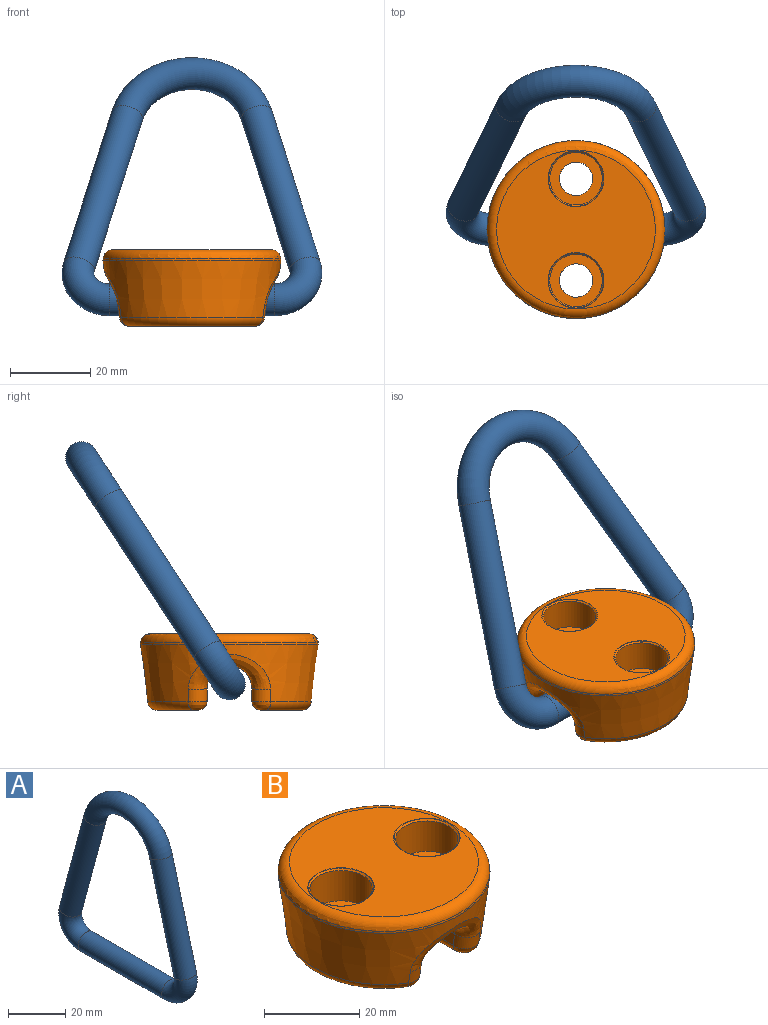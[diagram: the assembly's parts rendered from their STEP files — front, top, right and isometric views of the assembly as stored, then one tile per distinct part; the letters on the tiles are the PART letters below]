
ASSEMBLY  parts=2 mates=1
PART A: 6 faces, bbox 7.9x66.8x78.1 mm
  f0: cylinder r=3.97mm len=47.18mm, axis (0,0.26,0.97), area 1164.9mm2, adj f1,f5
  f1: torus R=7.94mm, axis (-1,0,0), area 362.7mm2, adj f0,f2
  f2: cylinder r=3.97mm len=41.05mm, axis (0,-1,0), area 1023.6mm2, adj f1,f3
  f3: torus R=7.94mm, axis (-1,0,0), area 362.7mm2, adj f2,f4
  f4: cylinder r=3.97mm len=47.18mm, axis (0,0.26,-0.97), area 1164.9mm2, adj f3,f5
  f5: torus R=16.67mm, axis (1,0,0), area 1088.2mm2, adj f0,f4
PART B: 44 faces, bbox 48x48x32 mm
  f0: plane 39.61x39.61mm, normal (0,0,1), area 926.8mm2, adj f22,f42,f43
  f1: cylinder r=5.56mm len=30.74mm, axis (0,1,0), area 274.6mm2, adj f6,f7,f9,f12,f32,f33,f34,f35
  f2: plane 31.44x10.14mm, normal (0,0,-1), area 170mm2, adj f14,f15,f16,f17,f39
  f3: cone r=22.23mm half-angle=7deg, axis (0,0,-1), area 63.1mm2, adj f4,f22
  f4: cone r=22.23mm half-angle=7deg, axis (0,0,1), area 1520.3mm2, adj f3,f8,f9,f10,f11,f12,f13,f16
  f5: plane 31.44x10.14mm, normal (0,0,-1), area 170mm2, adj f18,f19,f20,f21,f38
  f6: plane 30.74x3.18mm, normal (1,0,0), area 96.2mm2, adj f1,f8,f13,f15
  f7: plane 30.74x3.18mm, normal (-1,0,0), area 96.2mm2, adj f1,f10,f11,f20
  f8: bspline ~26.1x8.53mm, area 21mm2, adj f4,f6,f9,f17
  f9: bspline ~20.6x10.49mm, area 128mm2, adj f1,f4,f8,f10
  f10: bspline ~32.03x9.37mm, area 20.9mm2, adj f4,f7,f9,f21
  f11: bspline ~26.1x8.53mm, area 21mm2, adj f4,f7,f12,f18
  f12: bspline ~20.6x10.49mm, area 128mm2, adj f1,f4,f11,f13
  f13: bspline ~32.03x9.37mm, area 20.9mm2, adj f4,f6,f12,f14
  f14: bspline ~5.36x3.34mm, area 16.6mm2, adj f2,f13,f15,f16
  f15: cylinder r=2.39mm len=29.84mm, axis (0,-1,0), area 111.9mm2, adj f2,f6,f14,f17
  f16: torus R=18.09mm, axis (0,0,-1), area 140.7mm2, adj f2,f4,f14,f17
  f17: bspline ~5.37x3.89mm, area 16.6mm2, adj f2,f8,f15,f16
  f18: bspline ~5.37x3.89mm, area 16.6mm2, adj f5,f11,f19,f20
  f19: torus R=18.09mm, axis (0,0,-1), area 140.7mm2, adj f4,f5,f18,f21
  f20: cylinder r=2.39mm len=29.84mm, axis (0,1,0), area 111.9mm2, adj f5,f7,f18,f21
  f21: bspline ~5.36x3.34mm, area 16.6mm2, adj f5,f10,f19,f20
  f22: torus R=19.81mm, axis (0,0,1), area 460.6mm2, adj f0,f3
  f23: cylinder r=6.54mm len=13.08mm, axis (0,0,1), area 320.5mm2, adj f24,f41
  f24: plane 13.08x13.08mm, normal (0,0,1), area 79.9mm2, adj f23,f25
  f25: cylinder r=4.17mm len=10.49mm, axis (0,0,1), area 274.6mm2, adj f24,f38
  f26: cylinder r=6.54mm len=13.08mm, axis (0,0,1), area 320.5mm2, adj f27,f40
  f27: plane 13.08x13.08mm, normal (0,0,1), area 79.9mm2, adj f26,f28
  f28: cylinder r=4.17mm len=10.49mm, axis (0,0,1), area 274.6mm2, adj f27,f39
  f29: cylinder r=5.56mm len=14.86mm, axis (0,-1,0), area 273.5mm2, adj f30,f31,f32,f37
  f30: torus R=5.05mm, axis (0,-1,0), area 7.2mm2, adj f29,f34,f36
  f31: torus R=5.05mm, axis (0,-1,0), area 7.2mm2, adj f29,f33,f35
  f32: cylinder r=0.51mm len=14.86mm, axis (0,1,0), area 1.3mm2, adj f1,f29,f33,f34
  f33: bspline ~5.89x5.61mm, area 5mm2, adj f1,f31,f32,f35
  f34: bspline ~6.89x5.61mm, area 5mm2, adj f1,f30,f32,f36
  f35: bspline ~6.89x5.61mm, area 5mm2, adj f1,f31,f33,f37
  f36: bspline ~6.89x5.61mm, area 5mm2, adj f1,f30,f34,f37
  f37: cylinder r=0.51mm len=14.86mm, axis (0,-1,0), area 1.3mm2, adj f1,f29,f35,f36
  f38: cone r=4.55mm half-angle=45deg, axis (0,0,-1), area 14.7mm2, adj f5,f25
  f39: cone r=4.55mm half-angle=45deg, axis (0,0,-1), area 14.7mm2, adj f2,f28
  f40: cone r=6.54mm half-angle=45deg, axis (0,0,1), area 20.5mm2, adj f26,f43
  f41: cone r=6.54mm half-angle=45deg, axis (0,0,1), area 20.5mm2, adj f23,f42
  f42: torus R=6.97mm, axis (0,0,1), area 4.3mm2, adj f0,f41
  f43: torus R=6.97mm, axis (0,0,1), area 4.3mm2, adj f0,f40
PLACE A rot(axis=(-0.27,-0.27,-0.92),94.7deg) t=(0,36.94,63.03)mm
PLACE B rot(axis=(0,0,1),90deg) t=(0,0,16.51)mm fixed
MATE revolute A.f2 <-> B.f29  axis (-1,0,0) through (0,0,6.58)mm
